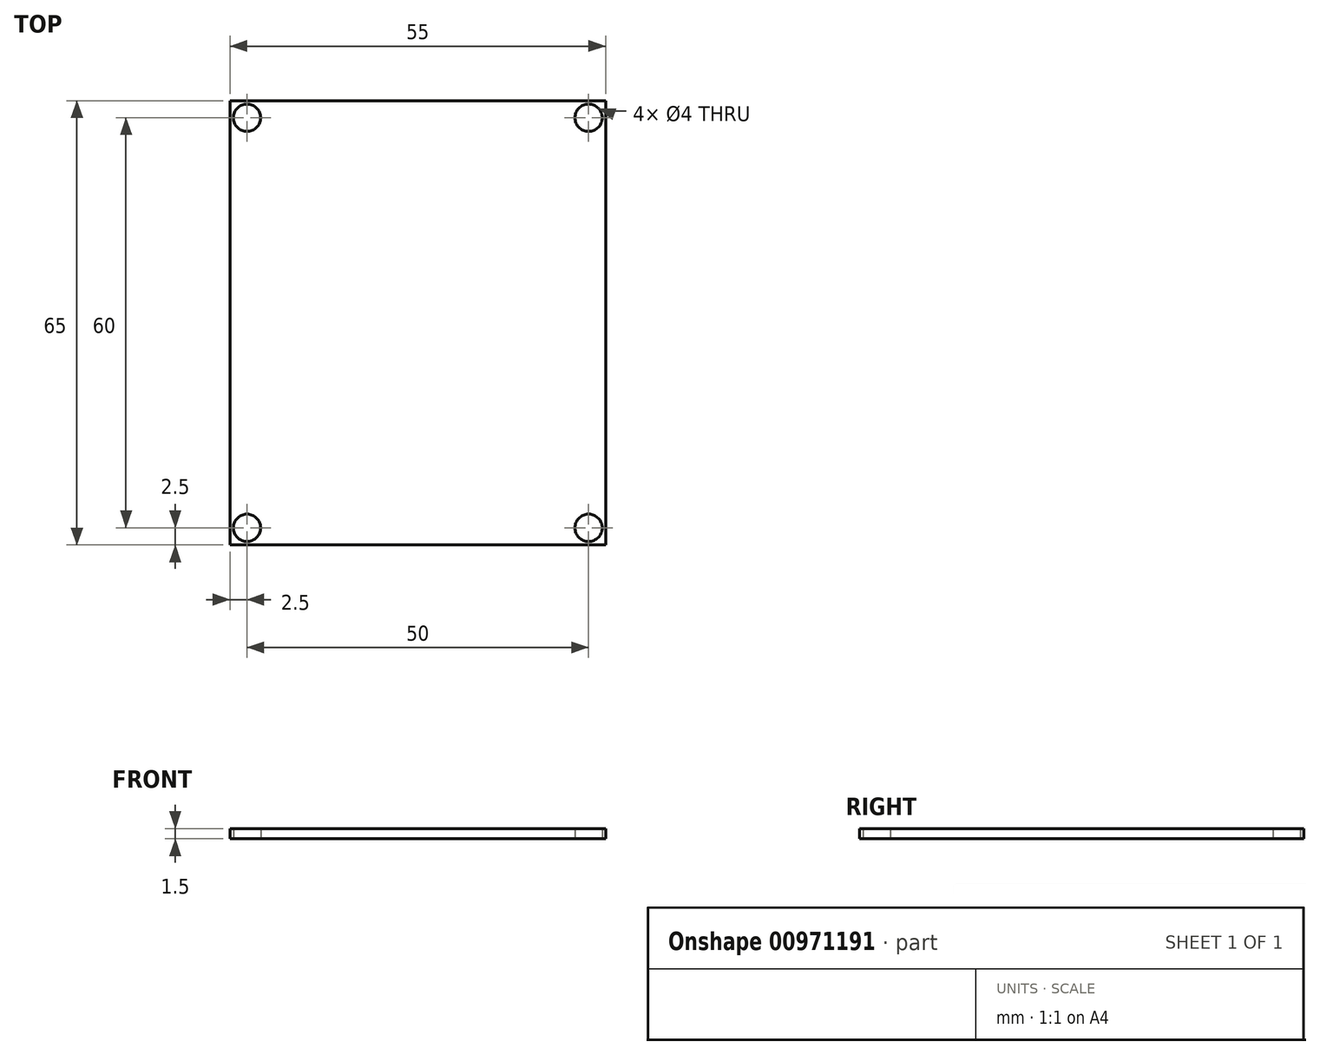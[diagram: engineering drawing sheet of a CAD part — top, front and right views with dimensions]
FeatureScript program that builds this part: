
annotation { "Feature Type Name" : "Feature", "Feature Type Description" : "" }
export const myFeature = defineFeature(function(context is Context, id is Id, definition is map)
    precondition{}
    {
        {
            var Q0;
            Q0=qCreatedBy(makeId("Top.planeOp"),FACE);
            var sketch = newSketch(context, id + "F0", { "sketchPlane" : qUnion([Q0])});
            skLineSegment(sketch, "E0.bottom", {"start": v(0, 0) * mm, "end": v(55, 0) * mm});
            skLineSegment(sketch, "E0.top", {"start": v(0, 65) * mm, "end": v(55, 65) * mm});
            skLineSegment(sketch, "E0.left", {"start": v(0, 0) * mm, "end": v(0, 65) * mm});
            skLineSegment(sketch, "E0.right", {"start": v(55, 0) * mm, "end": v(55, 65) * mm});
            skCircle(sketch, "E1", {"center": v(2.5, 62.5) * mm, "radius": 2 * mm});
            skCircle(sketch, "E2", {"center": v(52.5, 62.5) * mm, "radius": 2 * mm});
            skCircle(sketch, "E3", {"center": v(2.5, 2.5) * mm, "radius": 2 * mm});
            skCircle(sketch, "E4", {"center": v(52.5, 2.5) * mm, "radius": 2 * mm});
            skSolve(sketch);
        }
        {
            var Q0;
            Q0=makeQuery(id+"F0.imprint","IMPRINT",FACE,{"disambiguationData":[TD([[makeQuery(id+"F0.imprint","IMPRINT",EDGE,{"derivedFrom":sQuery(id+"F0.wireOp",EDGE,"E0.bottom")}),1.0]])]});
            extrude(context, id + "F1", {"entities" : qUnion([Q0]), "depth" : 1.5 * mm, "offsetDistance" : 25 * mm});
        }
    });
